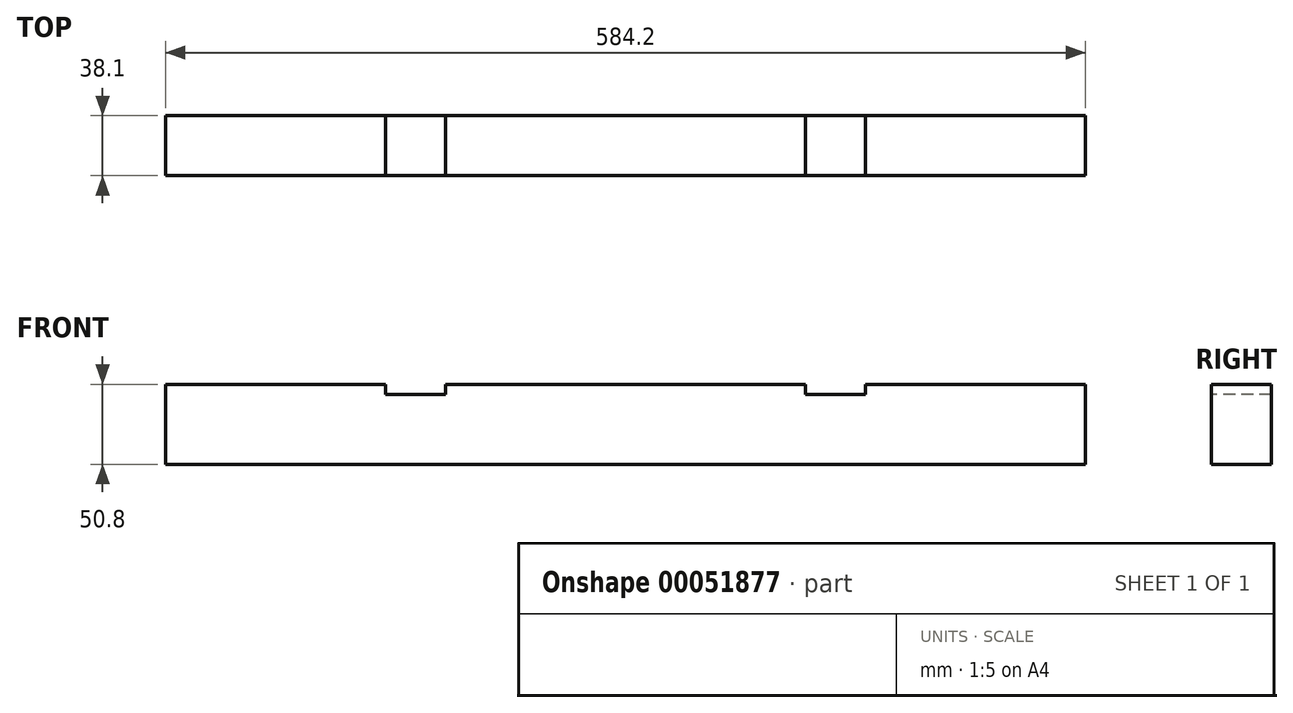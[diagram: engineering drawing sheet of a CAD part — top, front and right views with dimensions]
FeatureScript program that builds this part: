
annotation { "Feature Type Name" : "Feature", "Feature Type Description" : "" }
export const myFeature = defineFeature(function(context is Context, id is Id, definition is map)
    precondition{}
    {
        {
            var Q0;
            Q0=qCreatedBy(makeId("Right.planeOp"),FACE);
            var sketch = newSketch(context, id + "F0", { "sketchPlane" : qUnion([Q0])});
            skLineSegment(sketch, "E0.bottom", {"start": v(-19.05, 25.4) * mm, "end": v(19.05, 25.4) * mm});
            skLineSegment(sketch, "E0.top", {"start": v(-19.05, -25.4) * mm, "end": v(19.05, -25.4) * mm});
            skLineSegment(sketch, "E0.left", {"start": v(-19.05, 25.4) * mm, "end": v(-19.05, -25.4) * mm});
            skLineSegment(sketch, "E0.right", {"start": v(19.05, 25.4) * mm, "end": v(19.05, -25.4) * mm});
            skSolve(sketch);
        }
        {
            var Q0;
            Q0=makeQuery(id+"F0.imprint","IMPRINT",FACE,{"disambiguationData":[TD([[makeQuery(id+"F0.imprint","IMPRINT",EDGE,{"derivedFrom":sQuery(id+"F0.wireOp",EDGE,"E0.bottom")}),-1.0]])]});
            extrude(context, id + "F1", {"entities" : qUnion([Q0]), "depth" : 584.2 * mm});
        }
        {
            var Q0;
            Q0=makeQuery(id+"F1.opExtrude","SWEPT_FACE",FACE,{"disambiguationData":[OSD([sQuery(id+"F0.wireOp",EDGE,"E0.left")])]});
            var sketch = newSketch(context, id + "F2", { "sketchPlane" : qUnion([Q0])});
            skLineSegment(sketch, "E1.bottom", {"start": v(139.7, 25.4) * mm, "end": v(177.8, 25.4) * mm});
            skLineSegment(sketch, "E1.top", {"start": v(139.7, 19.05) * mm, "end": v(177.8, 19.05) * mm});
            skLineSegment(sketch, "E1.left", {"start": v(177.8, 25.4) * mm, "end": v(177.8, 19.05) * mm});
            skLineSegment(sketch, "E1.right", {"start": v(139.7, 25.4) * mm, "end": v(139.7, 19.05) * mm});
            skLineSegment(sketch, "E2.bottom", {"start": v(406.4, 25.4) * mm, "end": v(444.5, 25.4) * mm});
            skLineSegment(sketch, "E2.top", {"start": v(406.4, 19.05) * mm, "end": v(444.5, 19.05) * mm});
            skLineSegment(sketch, "E2.left", {"start": v(406.4, 25.4) * mm, "end": v(406.4, 19.05) * mm});
            skLineSegment(sketch, "E2.right", {"start": v(444.5, 25.4) * mm, "end": v(444.5, 19.05) * mm});
            skSolve(sketch);
        }
        {
            var Q0;
            Q0 = qSketchRegion(id + "F2", true);
            extrude(context, id + "F3", {"entities" : qUnion([Q0]), "operationType" : NewBodyOperationType.REMOVE, "endBound" : BoundingType.UP_TO_NEXT, "oppositeDirection" : true, "depth" : 25.4 * mm});
        }
    });
